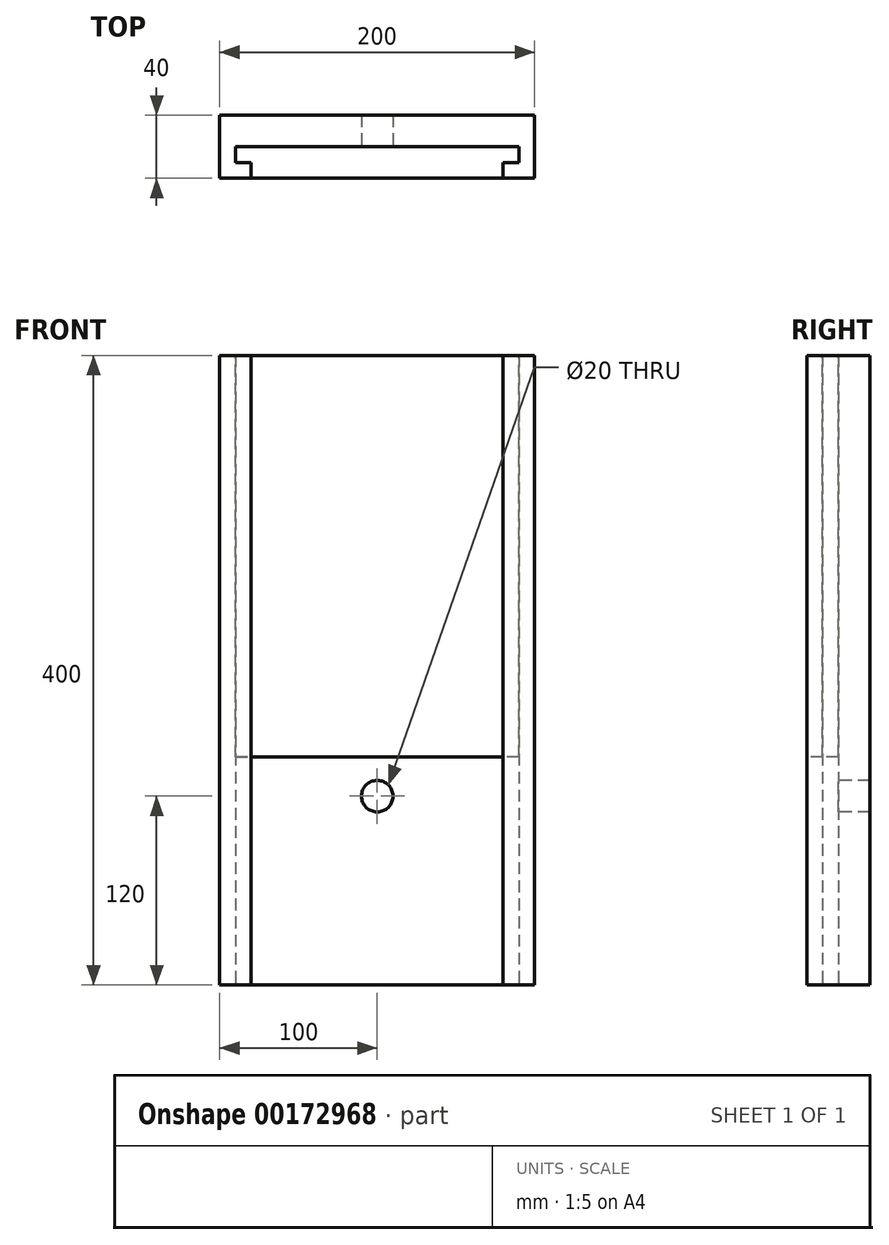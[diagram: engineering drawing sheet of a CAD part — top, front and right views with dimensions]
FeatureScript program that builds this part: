
annotation { "Feature Type Name" : "Feature", "Feature Type Description" : "" }
export const myFeature = defineFeature(function(context is Context, id is Id, definition is map)
    precondition{}
    {
        {
            var Q0;
            Q0=qCreatedBy(makeId("Top.planeOp"),FACE);
            var sketch = newSketch(context, id + "F0", { "sketchPlane" : qUnion([Q0])});
            skLineSegment(sketch, "E0", {"start": v(0, 20) * mm, "end": v(90, 20) * mm});
            skLineSegment(sketch, "E1", {"start": v(90, 20) * mm, "end": v(90, 10) * mm});
            skLineSegment(sketch, "E2", {"start": v(90, 10) * mm, "end": v(80, 10) * mm});
            skLineSegment(sketch, "E3", {"start": v(80, 10) * mm, "end": v(80, 0) * mm});
            skLineSegment(sketch, "E4", {"start": v(0, 40) * mm, "end": v(100, 40) * mm});
            skLineSegment(sketch, "E5", {"start": v(100, 40) * mm, "end": v(100, 0) * mm});
            skLineSegment(sketch, "E6", {"start": v(0, 40) * mm, "end": v(0, 0) * mm, "construction": true});
            skLineSegment(sketch, "E7.MirrorCS", {"start": v(0, 40) * mm, "end": v(-100, 40) * mm});
            skLineSegment(sketch, "E8.MirrorCS", {"start": v(0, 20) * mm, "end": v(-90, 20) * mm});
            skLineSegment(sketch, "E9.MirrorCS", {"start": v(-90, 20) * mm, "end": v(-90, 10) * mm});
            skLineSegment(sketch, "E10.MirrorCS", {"start": v(-90, 10) * mm, "end": v(-80, 10) * mm});
            skLineSegment(sketch, "E11.MirrorCS", {"start": v(-80, 10) * mm, "end": v(-80, 0) * mm});
            skLineSegment(sketch, "E12.MirrorCS", {"start": v(-100, 40) * mm, "end": v(-100, 0) * mm});
            skLineSegment(sketch, "E13", {"start": v(80, 0) * mm, "end": v(100, 0) * mm});
            skLineSegment(sketch, "E14.MirrorCS", {"start": v(-80, 0) * mm, "end": v(-100, 0) * mm});
            skSolve(sketch);
        }
        {
            var Q0;
            Q0 = qSketchRegion(id + "F0", true);
            extrude(context, id + "F1", {"entities" : qUnion([Q0]), "depth" : 280 * mm, "hasSecondDirection" : true, "secondDirectionOppositeDirection" : true, "secondDirectionDepth" : 120 * mm});
        }
        {
            var Q0;
            Q0=makeQuery(id+"F1.opExtrude","SWEPT_FACE",FACE,{"disambiguationData":[OSD([sQuery(id+"F0.wireOp",EDGE,"E0"),sQuery(id+"F0.wireOp",EDGE,"E8.MirrorCS")])]});
            var sketch = newSketch(context, id + "F2", { "sketchPlane" : qUnion([Q0])});
            skCircle(sketch, "E15", {"center": v(0, 0) * mm, "radius": 10 * mm});
            skSolve(sketch);
        }
        {
            var Q0;
            Q0 = qSketchRegion(id + "F2", true);
            extrude(context, id + "F3", {"entities" : qUnion([Q0]), "operationType" : NewBodyOperationType.REMOVE, "oppositeDirection" : true, "depth" : 20 * mm});
        }
        {
            var Q0;
            Q0=makeQuery(id+"F1.opExtrude","CAP_FACE",FACE,{"disambiguationData":[OSD([sQuery(id+"F0.wireOp",EDGE,"E0"),sQuery(id+"F0.wireOp",EDGE,"E1"),sQuery(id+"F0.wireOp",EDGE,"E2"),sQuery(id+"F0.wireOp",EDGE,"E3"),sQuery(id+"F0.wireOp",EDGE,"E4"),sQuery(id+"F0.wireOp",EDGE,"E5"),sQuery(id+"F0.wireOp",EDGE,"E7.MirrorCS"),sQuery(id+"F0.wireOp",EDGE,"E8.MirrorCS"),sQuery(id+"F0.wireOp",EDGE,"E9.MirrorCS"),sQuery(id+"F0.wireOp",EDGE,"E10.MirrorCS"),sQuery(id+"F0.wireOp",EDGE,"E11.MirrorCS"),sQuery(id+"F0.wireOp",EDGE,"E12.MirrorCS"),sQuery(id+"F0.wireOp",EDGE,"E13"),sQuery(id+"F0.wireOp",EDGE,"E14.MirrorCS")])],"isStart":false});
            var sketch = newSketch(context, id + "F4", { "sketchPlane" : qUnion([Q0])});
            skLineSegment(sketch, "E16", {"start": v(-90, 20) * mm, "end": v(-90, 10) * mm});
            skLineSegment(sketch, "E17", {"start": v(-90, 10) * mm, "end": v(-80, 10) * mm});
            skLineSegment(sketch, "E18", {"start": v(-80, 10) * mm, "end": v(-80, 0) * mm});
            skLineSegment(sketch, "E19", {"start": v(-80, 0) * mm, "end": v(80, 0) * mm});
            skLineSegment(sketch, "E20", {"start": v(80, 0) * mm, "end": v(80, 10) * mm});
            skLineSegment(sketch, "E21", {"start": v(80, 10) * mm, "end": v(90, 10) * mm});
            skLineSegment(sketch, "E22", {"start": v(90, 10) * mm, "end": v(90, 20) * mm});
            skLineSegment(sketch, "E23", {"start": v(90, 20) * mm, "end": v(-90, 20) * mm});
            skSolve(sketch);
        }
        {
            var Q0;
            Q0 = qSketchRegion(id + "F4", true);
            extrude(context, id + "F5", {"entities" : qUnion([Q0]), "oppositeDirection" : true, "depth" : 255 * mm});
        }
    });
